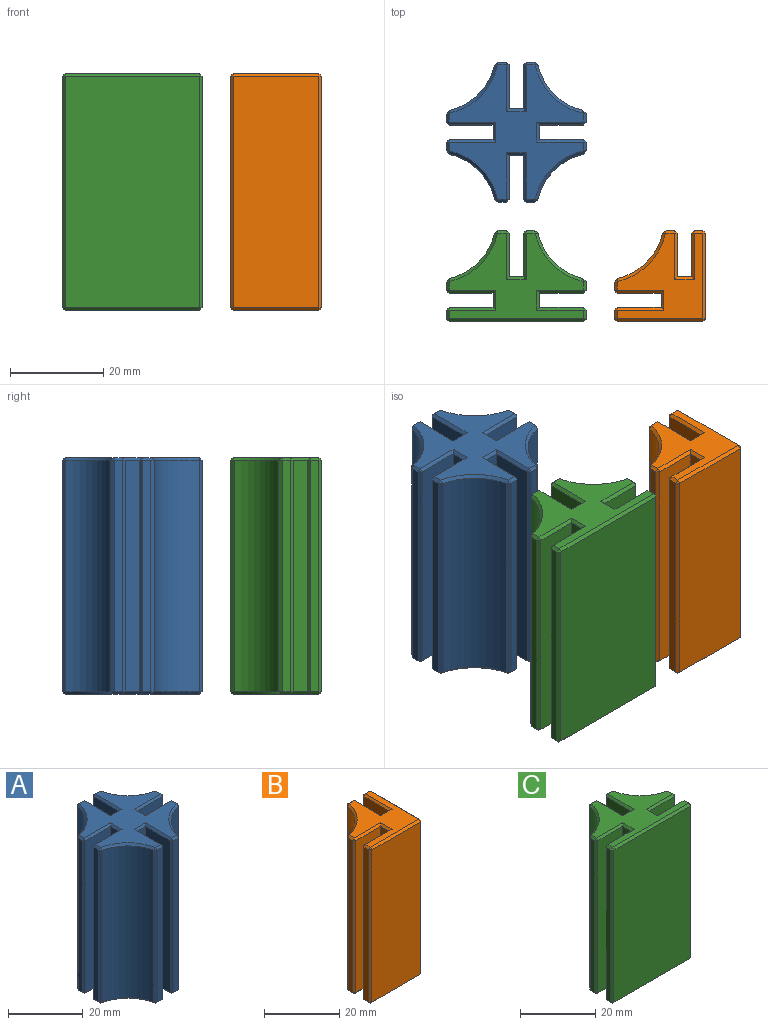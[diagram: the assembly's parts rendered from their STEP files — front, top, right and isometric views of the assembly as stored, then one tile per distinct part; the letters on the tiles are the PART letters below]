
ASSEMBLY  parts=3 mates=2
PART A: 122 faces, bbox 30x30x50.8 mm
  f0: plane 49.6x1.66mm, normal (-1,0,0), area 82.3mm2, adj f98,f106,f107,f108
  f1: plane 49.6x9.4mm, normal (0,-1,0), area 466.2mm2, adj f2,f97,f98,f99
  f2: plane 49.6x3.08mm, normal (-1,0,0), area 152.5mm2, adj f1,f3,f93,f94
  f3: plane 49.6x9.4mm, normal (0,1,0), area 466.2mm2, adj f2,f79,f88,f89
  f4: plane 49.6x1.8mm, normal (-1,0,0), area 89.3mm2, adj f69,f78,f79,f80
  f5: cylinder r=12.91mm len=49.6mm, axis (0,0,-1), area 712.6mm2, adj f59,f68,f69,f70
  f6: plane 49.6x1.66mm, normal (0,-1,0), area 82.3mm2, adj f50,f58,f59,f60
  f7: plane 49.6x9.4mm, normal (1,0,0), area 466.2mm2, adj f8,f49,f50,f51
  f8: plane 49.6x3.08mm, normal (0,-1,0), area 152.5mm2, adj f7,f9,f45,f46
  f9: plane 49.6x9.4mm, normal (-1,0,0), area 466.2mm2, adj f8,f31,f40,f41
  f10: plane 49.6x1.8mm, normal (0,-1,0), area 89.3mm2, adj f26,f30,f31,f32
  f11: cylinder r=12.91mm len=49.6mm, axis (0,0,-1), area 712.6mm2, adj f26,f29,f33,f34
  f12: plane 49.6x1.66mm, normal (1,0,0), area 82.3mm2, adj f34,f39,f42,f43
  f13: plane 49.6x9.4mm, normal (0,1,0), area 466.2mm2, adj f14,f43,f48,f52
  f14: plane 49.6x3.08mm, normal (1,0,0), area 152.5mm2, adj f13,f15,f53,f56
  f15: plane 49.6x9.4mm, normal (0,-1,0), area 466.2mm2, adj f14,f57,f61,f62
  f16: plane 49.6x1.8mm, normal (1,0,0), area 89.3mm2, adj f62,f67,f71,f72
  f17: cylinder r=12.91mm len=49.6mm, axis (0,0,-1), area 712.6mm2, adj f72,f77,f81,f82
  f18: plane 49.6x1.66mm, normal (0,1,0), area 82.3mm2, adj f82,f87,f90,f91
  f19: plane 49.6x9.4mm, normal (-1,0,0), area 466.2mm2, adj f20,f91,f96,f100
  f20: plane 49.6x3.08mm, normal (0,1,0), area 152.5mm2, adj f19,f21,f101,f104
  f21: plane 49.6x9.4mm, normal (1,0,0), area 466.2mm2, adj f20,f105,f109,f110
  f22: plane 49.6x1.8mm, normal (0,1,0), area 89.3mm2, adj f110,f115,f118,f121
  f23: cylinder r=12.91mm len=49.6mm, axis (0,0,-1), area 712.6mm2, adj f107,f116,f117,f121
  f24: plane 28.8x28.8mm, normal (0,0,1), area 358.3mm2, adj f29,f30,f39,f40,f45,f48,f49,f53
  f25: plane 28.8x28.8mm, normal (0,0,-1), area 358.3mm2, adj f32,f33,f41,f42,f46,f51,f52,f56
  f26: plane 49.6x0.76mm, normal (0.71,-0.71,0), area 53.2mm2, adj f10,f11,f27,f28
  f27: plane 0.77x0.77mm, normal (0.61,-0.61,0.5), area 0.4mm2, adj f26,f29,f30
  f28: plane 0.77x0.77mm, normal (0.61,-0.61,-0.5), area 0.4mm2, adj f26,f32,f33
  f29: cone r=13.51mm half-angle=45deg, axis (0,0,1), area 12.7mm2, adj f11,f24,f27,f35
  f30: plane 1.91x0.6mm, normal (0,-0.71,0.71), area 1.6mm2, adj f10,f24,f27,f36
  f31: plane 49.6x0.6mm, normal (-0.71,-0.71,0), area 42.1mm2, adj f9,f10,f36,f37
  f32: plane 1.91x0.6mm, normal (0,-0.71,-0.71), area 1.6mm2, adj f10,f25,f28,f37
  f33: cone r=12.91mm half-angle=45deg, axis (0,0,-1), area 12.7mm2, adj f11,f25,f28,f38
  f34: plane 49.6x0.86mm, normal (0.82,-0.57,0), area 52.2mm2, adj f11,f12,f35,f38
  f35: plane 0.87x0.61mm, normal (0.71,-0.49,0.5), area 0.4mm2, adj f29,f34,f39
  f36: plane 0.6x0.6mm, normal (-0.58,-0.58,0.58), area 0.3mm2, adj f30,f31,f40
  f37: plane 0.6x0.6mm, normal (-0.58,-0.58,-0.58), area 0.3mm2, adj f31,f32,f41
  f38: plane 0.87x0.61mm, normal (0.71,-0.49,-0.5), area 0.4mm2, adj f33,f34,f42
  f39: plane 1.91x0.6mm, normal (0.71,0,0.71), area 1.5mm2, adj f12,f24,f35,f44
  f40: plane 10x0.6mm, normal (-0.71,0,0.71), area 8.2mm2, adj f9,f24,f36,f45
  f41: plane 10x0.6mm, normal (-0.71,0,-0.71), area 8.2mm2, adj f9,f25,f37,f46
  f42: plane 1.91x0.6mm, normal (0.71,0,-0.71), area 1.5mm2, adj f12,f25,f38,f47
  f43: plane 49.6x0.6mm, normal (0.71,0.71,0), area 42.1mm2, adj f12,f13,f44,f47
  f44: plane 0.6x0.6mm, normal (0.58,0.58,0.58), area 0.3mm2, adj f39,f43,f48
  f45: plane 4.28x0.6mm, normal (0,-0.71,0.71), area 3.1mm2, adj f8,f24,f40,f49
  f46: plane 4.28x0.6mm, normal (0,-0.71,-0.71), area 3.1mm2, adj f8,f25,f41,f51
  f47: plane 0.6x0.6mm, normal (0.58,0.58,-0.58), area 0.3mm2, adj f42,f43,f52
  f48: plane 10x0.6mm, normal (0,0.71,0.71), area 8.2mm2, adj f13,f24,f44,f53
  f49: plane 10x0.6mm, normal (0.71,0,0.71), area 8.2mm2, adj f7,f24,f45,f54
  f50: plane 49.6x0.6mm, normal (0.71,-0.71,0), area 42.1mm2, adj f6,f7,f54,f55
  f51: plane 10x0.6mm, normal (0.71,0,-0.71), area 8.2mm2, adj f7,f25,f46,f55
  f52: plane 10x0.6mm, normal (0,0.71,-0.71), area 8.2mm2, adj f13,f25,f47,f56
  f53: plane 4.28x0.6mm, normal (0.71,0,0.71), area 3.1mm2, adj f14,f24,f48,f57
  f54: plane 0.6x0.6mm, normal (0.58,-0.58,0.58), area 0.3mm2, adj f49,f50,f58
  f55: plane 0.6x0.6mm, normal (0.58,-0.58,-0.58), area 0.3mm2, adj f50,f51,f60
  f56: plane 4.28x0.6mm, normal (0.71,0,-0.71), area 3.1mm2, adj f14,f25,f52,f61
  f57: plane 10x0.6mm, normal (0,-0.71,0.71), area 8.2mm2, adj f15,f24,f53,f63
  f58: plane 1.91x0.6mm, normal (0,-0.71,0.71), area 1.5mm2, adj f6,f24,f54,f64
  f59: plane 49.6x0.86mm, normal (-0.57,-0.82,0), area 52.2mm2, adj f5,f6,f64,f65
  f60: plane 1.91x0.6mm, normal (0,-0.71,-0.71), area 1.5mm2, adj f6,f25,f55,f65
  f61: plane 10x0.6mm, normal (0,-0.71,-0.71), area 8.2mm2, adj f15,f25,f56,f66
  f62: plane 49.6x0.6mm, normal (0.71,-0.71,0), area 42.1mm2, adj f15,f16,f63,f66
  f63: plane 0.6x0.6mm, normal (0.58,-0.58,0.58), area 0.3mm2, adj f57,f62,f67
  f64: plane 0.87x0.61mm, normal (-0.49,-0.71,0.5), area 0.4mm2, adj f58,f59,f68
  f65: plane 0.87x0.61mm, normal (-0.49,-0.71,-0.5), area 0.4mm2, adj f59,f60,f70
  f66: plane 0.6x0.6mm, normal (0.58,-0.58,-0.58), area 0.3mm2, adj f61,f62,f71
  f67: plane 1.91x0.6mm, normal (0.71,0,0.71), area 1.6mm2, adj f16,f24,f63,f73
  f68: cone r=13.51mm half-angle=45deg, axis (0,0,1), area 12.7mm2, adj f5,f24,f64,f74
  f69: plane 49.6x0.76mm, normal (-0.71,-0.71,0), area 53.2mm2, adj f4,f5,f74,f75
  f70: cone r=12.91mm half-angle=45deg, axis (0,0,-1), area 12.7mm2, adj f5,f25,f65,f75
  f71: plane 1.91x0.6mm, normal (0.71,0,-0.71), area 1.6mm2, adj f16,f25,f66,f76
  f72: plane 49.6x0.76mm, normal (0.71,0.71,0), area 53.2mm2, adj f16,f17,f73,f76
  f73: plane 0.77x0.77mm, normal (0.61,0.61,0.5), area 0.4mm2, adj f67,f72,f77
  f74: plane 0.77x0.77mm, normal (-0.61,-0.61,0.5), area 0.4mm2, adj f68,f69,f78
  f75: plane 0.77x0.77mm, normal (-0.61,-0.61,-0.5), area 0.4mm2, adj f69,f70,f80
  f76: plane 0.77x0.77mm, normal (0.61,0.61,-0.5), area 0.4mm2, adj f71,f72,f81
  f77: cone r=13.51mm half-angle=45deg, axis (0,0,1), area 12.7mm2, adj f17,f24,f73,f83
  f78: plane 1.91x0.6mm, normal (-0.71,0,0.71), area 1.6mm2, adj f4,f24,f74,f84
  f79: plane 49.6x0.6mm, normal (-0.71,0.71,0), area 42.1mm2, adj f3,f4,f84,f85
  f80: plane 1.91x0.6mm, normal (-0.71,0,-0.71), area 1.6mm2, adj f4,f25,f75,f85
  f81: cone r=12.91mm half-angle=45deg, axis (0,0,-1), area 12.7mm2, adj f17,f25,f76,f86
  f82: plane 49.6x0.86mm, normal (0.57,0.82,0), area 52.2mm2, adj f17,f18,f83,f86
  f83: plane 0.87x0.61mm, normal (0.49,0.71,0.5), area 0.4mm2, adj f77,f82,f87
  f84: plane 0.6x0.6mm, normal (-0.58,0.58,0.58), area 0.3mm2, adj f78,f79,f88
  f85: plane 0.6x0.6mm, normal (-0.58,0.58,-0.58), area 0.3mm2, adj f79,f80,f89
  f86: plane 0.87x0.61mm, normal (0.49,0.71,-0.5), area 0.4mm2, adj f81,f82,f90
  f87: plane 1.91x0.6mm, normal (0,0.71,0.71), area 1.5mm2, adj f18,f24,f83,f92
  f88: plane 10x0.6mm, normal (0,0.71,0.71), area 8.2mm2, adj f3,f24,f84,f93
  f89: plane 10x0.6mm, normal (0,0.71,-0.71), area 8.2mm2, adj f3,f25,f85,f94
  f90: plane 1.91x0.6mm, normal (0,0.71,-0.71), area 1.5mm2, adj f18,f25,f86,f95
  f91: plane 49.6x0.6mm, normal (-0.71,0.71,0), area 42.1mm2, adj f18,f19,f92,f95
  f92: plane 0.6x0.6mm, normal (-0.58,0.58,0.58), area 0.3mm2, adj f87,f91,f96
  f93: plane 4.28x0.6mm, normal (-0.71,0,0.71), area 3.1mm2, adj f2,f24,f88,f97
  f94: plane 4.28x0.6mm, normal (-0.71,0,-0.71), area 3.1mm2, adj f2,f25,f89,f99
  f95: plane 0.6x0.6mm, normal (-0.58,0.58,-0.58), area 0.3mm2, adj f90,f91,f100
  f96: plane 10x0.6mm, normal (-0.71,0,0.71), area 8.2mm2, adj f19,f24,f92,f101
  f97: plane 10x0.6mm, normal (0,-0.71,0.71), area 8.2mm2, adj f1,f24,f93,f102
  f98: plane 49.6x0.6mm, normal (-0.71,-0.71,0), area 42.1mm2, adj f0,f1,f102,f103
  f99: plane 10x0.6mm, normal (0,-0.71,-0.71), area 8.2mm2, adj f1,f25,f94,f103
  f100: plane 10x0.6mm, normal (-0.71,0,-0.71), area 8.2mm2, adj f19,f25,f95,f104
  f101: plane 4.28x0.6mm, normal (0,0.71,0.71), area 3.1mm2, adj f20,f24,f96,f105
  f102: plane 0.6x0.6mm, normal (-0.58,-0.58,0.58), area 0.3mm2, adj f97,f98,f106
  f103: plane 0.6x0.6mm, normal (-0.58,-0.58,-0.58), area 0.3mm2, adj f98,f99,f108
  f104: plane 4.28x0.6mm, normal (0,0.71,-0.71), area 3.1mm2, adj f20,f25,f100,f109
  f105: plane 10x0.6mm, normal (0.71,0,0.71), area 8.2mm2, adj f21,f24,f101,f111
  f106: plane 1.91x0.6mm, normal (-0.71,0,0.71), area 1.5mm2, adj f0,f24,f102,f112
  f107: plane 49.6x0.86mm, normal (-0.82,0.57,0), area 52.2mm2, adj f0,f23,f112,f113
  f108: plane 1.91x0.6mm, normal (-0.71,0,-0.71), area 1.5mm2, adj f0,f25,f103,f113
  f109: plane 10x0.6mm, normal (0.71,0,-0.71), area 8.2mm2, adj f21,f25,f104,f114
  f110: plane 49.6x0.6mm, normal (0.71,0.71,0), area 42.1mm2, adj f21,f22,f111,f114
  f111: plane 0.6x0.6mm, normal (0.58,0.58,0.58), area 0.3mm2, adj f105,f110,f115
  f112: plane 0.87x0.61mm, normal (-0.71,0.49,0.5), area 0.4mm2, adj f106,f107,f116
  f113: plane 0.87x0.61mm, normal (-0.71,0.49,-0.5), area 0.4mm2, adj f107,f108,f117
  f114: plane 0.6x0.6mm, normal (0.58,0.58,-0.58), area 0.3mm2, adj f109,f110,f118
  f115: plane 1.91x0.6mm, normal (0,0.71,0.71), area 1.6mm2, adj f22,f24,f111,f119
  f116: cone r=13.51mm half-angle=45deg, axis (0,0,1), area 12.7mm2, adj f23,f24,f112,f119
  f117: cone r=12.91mm half-angle=45deg, axis (0,0,-1), area 12.7mm2, adj f23,f25,f113,f120
  f118: plane 1.91x0.6mm, normal (0,0.71,-0.71), area 1.6mm2, adj f22,f25,f114,f120
  f119: plane 0.77x0.77mm, normal (-0.61,0.61,0.5), area 0.4mm2, adj f115,f116,f121
  f120: plane 0.77x0.77mm, normal (-0.61,0.61,-0.5), area 0.4mm2, adj f117,f118,f121
  f121: plane 49.6x0.76mm, normal (-0.71,0.71,0), area 53.2mm2, adj f22,f23,f119,f120
PART B: 68 faces, bbox 19.5x19.5x50.8 mm
  f0: plane 49.6x1.66mm, normal (-1,0,0), area 82.3mm2, adj f44,f52,f53,f54
  f1: plane 49.6x9.4mm, normal (0,-1,0), area 466.2mm2, adj f2,f43,f44,f45
  f2: plane 49.6x3.08mm, normal (-1,0,0), area 152.5mm2, adj f1,f3,f39,f40
  f3: plane 49.6x9.4mm, normal (0,1,0), area 466.2mm2, adj f2,f25,f34,f35
  f4: plane 49.6x1.8mm, normal (-1,0,0), area 89.3mm2, adj f16,f24,f25,f26
  f5: plane 49.6x18.34mm, normal (0,-1,0), area 909.5mm2, adj f15,f16,f17,f18
  f6: plane 49.6x18.34mm, normal (1,0,0), area 909.5mm2, adj f18,f23,f27,f28
  f7: plane 49.6x1.8mm, normal (0,1,0), area 89.3mm2, adj f28,f33,f36,f37
  f8: plane 49.6x9.4mm, normal (-1,0,0), area 466.2mm2, adj f9,f37,f42,f46
  f9: plane 49.6x3.08mm, normal (0,1,0), area 152.5mm2, adj f8,f10,f47,f50
  f10: plane 49.6x9.4mm, normal (1,0,0), area 466.2mm2, adj f9,f51,f55,f56
  f11: plane 49.6x1.8mm, normal (0,1,0), area 89.3mm2, adj f56,f61,f64,f67
  f12: cylinder r=12.91mm len=49.6mm, axis (0,0,-1), area 712.6mm2, adj f53,f62,f63,f67
  f13: plane 18.34x18.34mm, normal (0,0,1), area 175.7mm2, adj f15,f23,f24,f33,f34,f39,f42,f43
  f14: plane 18.34x18.34mm, normal (0,0,-1), area 175.7mm2, adj f17,f26,f27,f35,f36,f40,f45,f46
  f15: plane 18.34x0.6mm, normal (0,-0.71,0.71), area 15.6mm2, adj f5,f13,f19,f20
  f16: plane 49.6x0.6mm, normal (-0.71,-0.71,0), area 42.1mm2, adj f4,f5,f20,f21
  f17: plane 18.34x0.6mm, normal (0,-0.71,-0.71), area 15.6mm2, adj f5,f14,f21,f22
  f18: plane 49.6x0.6mm, normal (0.71,-0.71,0), area 42.1mm2, adj f5,f6,f19,f22
  f19: plane 0.6x0.6mm, normal (0.58,-0.58,0.58), area 0.3mm2, adj f15,f18,f23
  f20: plane 0.6x0.6mm, normal (-0.58,-0.58,0.58), area 0.3mm2, adj f15,f16,f24
  f21: plane 0.6x0.6mm, normal (-0.58,-0.58,-0.58), area 0.3mm2, adj f16,f17,f26
  f22: plane 0.6x0.6mm, normal (0.58,-0.58,-0.58), area 0.3mm2, adj f17,f18,f27
  f23: plane 18.34x0.6mm, normal (0.71,0,0.71), area 15.6mm2, adj f6,f13,f19,f29
  f24: plane 1.8x0.6mm, normal (-0.71,0,0.71), area 1.5mm2, adj f4,f13,f20,f30
  f25: plane 49.6x0.6mm, normal (-0.71,0.71,0), area 42.1mm2, adj f3,f4,f30,f31
  f26: plane 1.8x0.6mm, normal (-0.71,0,-0.71), area 1.5mm2, adj f4,f14,f21,f31
  f27: plane 18.34x0.6mm, normal (0.71,0,-0.71), area 15.6mm2, adj f6,f14,f22,f32
  f28: plane 49.6x0.6mm, normal (0.71,0.71,0), area 42.1mm2, adj f6,f7,f29,f32
  f29: plane 0.6x0.6mm, normal (0.58,0.58,0.58), area 0.3mm2, adj f23,f28,f33
  f30: plane 0.6x0.6mm, normal (-0.58,0.58,0.58), area 0.3mm2, adj f24,f25,f34
  f31: plane 0.6x0.6mm, normal (-0.58,0.58,-0.58), area 0.3mm2, adj f25,f26,f35
  f32: plane 0.6x0.6mm, normal (0.58,0.58,-0.58), area 0.3mm2, adj f27,f28,f36
  f33: plane 1.8x0.6mm, normal (0,0.71,0.71), area 1.5mm2, adj f7,f13,f29,f38
  f34: plane 10x0.6mm, normal (0,0.71,0.71), area 8.2mm2, adj f3,f13,f30,f39
  f35: plane 10x0.6mm, normal (0,0.71,-0.71), area 8.2mm2, adj f3,f14,f31,f40
  f36: plane 1.8x0.6mm, normal (0,0.71,-0.71), area 1.5mm2, adj f7,f14,f32,f41
  f37: plane 49.6x0.6mm, normal (-0.71,0.71,0), area 42.1mm2, adj f7,f8,f38,f41
  f38: plane 0.6x0.6mm, normal (-0.58,0.58,0.58), area 0.3mm2, adj f33,f37,f42
  f39: plane 4.28x0.6mm, normal (-0.71,0,0.71), area 3.1mm2, adj f2,f13,f34,f43
  f40: plane 4.28x0.6mm, normal (-0.71,0,-0.71), area 3.1mm2, adj f2,f14,f35,f45
  f41: plane 0.6x0.6mm, normal (-0.58,0.58,-0.58), area 0.3mm2, adj f36,f37,f46
  f42: plane 10x0.6mm, normal (-0.71,0,0.71), area 8.2mm2, adj f8,f13,f38,f47
  f43: plane 10x0.6mm, normal (0,-0.71,0.71), area 8.2mm2, adj f1,f13,f39,f48
  f44: plane 49.6x0.6mm, normal (-0.71,-0.71,0), area 42.1mm2, adj f0,f1,f48,f49
  f45: plane 10x0.6mm, normal (0,-0.71,-0.71), area 8.2mm2, adj f1,f14,f40,f49
  f46: plane 10x0.6mm, normal (-0.71,0,-0.71), area 8.2mm2, adj f8,f14,f41,f50
  f47: plane 4.28x0.6mm, normal (0,0.71,0.71), area 3.1mm2, adj f9,f13,f42,f51
  f48: plane 0.6x0.6mm, normal (-0.58,-0.58,0.58), area 0.3mm2, adj f43,f44,f52
  f49: plane 0.6x0.6mm, normal (-0.58,-0.58,-0.58), area 0.3mm2, adj f44,f45,f54
  f50: plane 4.28x0.6mm, normal (0,0.71,-0.71), area 3.1mm2, adj f9,f14,f46,f55
  f51: plane 10x0.6mm, normal (0.71,0,0.71), area 8.2mm2, adj f10,f13,f47,f57
  f52: plane 1.91x0.6mm, normal (-0.71,0,0.71), area 1.5mm2, adj f0,f13,f48,f58
  f53: plane 49.6x0.86mm, normal (-0.82,0.57,0), area 52.2mm2, adj f0,f12,f58,f59
  f54: plane 1.91x0.6mm, normal (-0.71,0,-0.71), area 1.5mm2, adj f0,f14,f49,f59
  f55: plane 10x0.6mm, normal (0.71,0,-0.71), area 8.2mm2, adj f10,f14,f50,f60
  f56: plane 49.6x0.6mm, normal (0.71,0.71,0), area 42.1mm2, adj f10,f11,f57,f60
  f57: plane 0.6x0.6mm, normal (0.58,0.58,0.58), area 0.3mm2, adj f51,f56,f61
  f58: plane 0.87x0.61mm, normal (-0.71,0.49,0.5), area 0.4mm2, adj f52,f53,f62
  f59: plane 0.87x0.61mm, normal (-0.71,0.49,-0.5), area 0.4mm2, adj f53,f54,f63
  f60: plane 0.6x0.6mm, normal (0.58,0.58,-0.58), area 0.3mm2, adj f55,f56,f64
  f61: plane 1.91x0.6mm, normal (0,0.71,0.71), area 1.6mm2, adj f11,f13,f57,f65
  f62: cone r=13.51mm half-angle=45deg, axis (0,0,1), area 12.7mm2, adj f12,f13,f58,f65
  f63: cone r=12.91mm half-angle=45deg, axis (0,0,-1), area 12.7mm2, adj f12,f14,f59,f66
  f64: plane 1.91x0.6mm, normal (0,0.71,-0.71), area 1.6mm2, adj f11,f14,f60,f66
  f65: plane 0.77x0.77mm, normal (-0.61,0.61,0.5), area 0.4mm2, adj f61,f62,f67
  f66: plane 0.77x0.77mm, normal (-0.61,0.61,-0.5), area 0.4mm2, adj f63,f64,f67
  f67: plane 49.6x0.76mm, normal (-0.71,0.71,0), area 53.2mm2, adj f11,f12,f65,f66
PART C: 92 faces, bbox 30x19.5x50.8 mm
  f0: plane 49.6x1.66mm, normal (-1,0,0), area 82.3mm2, adj f68,f76,f77,f78
  f1: plane 49.6x9.4mm, normal (0,-1,0), area 466.2mm2, adj f2,f67,f68,f69
  f2: plane 49.6x3.08mm, normal (-1,0,0), area 152.5mm2, adj f1,f3,f63,f64
  f3: plane 49.6x9.4mm, normal (0,1,0), area 466.2mm2, adj f2,f49,f58,f59
  f4: plane 49.6x1.8mm, normal (-1,0,0), area 89.3mm2, adj f39,f48,f49,f50
  f5: plane 49.6x28.8mm, normal (0,-1,0), area 1428.5mm2, adj f29,f38,f39,f40
  f6: plane 49.6x1.8mm, normal (1,0,0), area 89.3mm2, adj f21,f28,f29,f30
  f7: plane 49.6x9.4mm, normal (0,1,0), area 466.2mm2, adj f8,f20,f21,f22
  f8: plane 49.6x3.08mm, normal (1,0,0), area 152.5mm2, adj f7,f9,f23,f26
  f9: plane 49.6x9.4mm, normal (0,-1,0), area 466.2mm2, adj f8,f27,f31,f32
  f10: plane 49.6x1.8mm, normal (1,0,0), area 89.3mm2, adj f32,f37,f41,f42
  f11: cylinder r=12.91mm len=49.6mm, axis (0,0,-1), area 712.6mm2, adj f42,f47,f51,f52
  f12: plane 49.6x1.66mm, normal (0,1,0), area 82.3mm2, adj f52,f57,f60,f61
  f13: plane 49.6x9.4mm, normal (-1,0,0), area 466.2mm2, adj f14,f61,f66,f70
  f14: plane 49.6x3.08mm, normal (0,1,0), area 152.5mm2, adj f13,f15,f71,f74
  f15: plane 49.6x9.4mm, normal (1,0,0), area 466.2mm2, adj f14,f75,f79,f80
  f16: plane 49.6x1.8mm, normal (0,1,0), area 89.3mm2, adj f80,f85,f88,f91
  f17: cylinder r=12.91mm len=49.6mm, axis (0,0,-1), area 712.6mm2, adj f77,f86,f87,f91
  f18: plane 28.8x18.34mm, normal (0,0,1), area 249.8mm2, adj f20,f23,f27,f28,f37,f38,f47,f48
  f19: plane 28.8x18.34mm, normal (0,0,-1), area 249.8mm2, adj f22,f26,f30,f31,f40,f41,f50,f51
  f20: plane 10x0.6mm, normal (0,0.71,0.71), area 8.2mm2, adj f7,f18,f23,f24
  f21: plane 49.6x0.6mm, normal (0.71,0.71,0), area 42.1mm2, adj f6,f7,f24,f25
  f22: plane 10x0.6mm, normal (0,0.71,-0.71), area 8.2mm2, adj f7,f19,f25,f26
  f23: plane 4.28x0.6mm, normal (0.71,0,0.71), area 3.1mm2, adj f8,f18,f20,f27
  f24: plane 0.6x0.6mm, normal (0.58,0.58,0.58), area 0.3mm2, adj f20,f21,f28
  f25: plane 0.6x0.6mm, normal (0.58,0.58,-0.58), area 0.3mm2, adj f21,f22,f30
  f26: plane 4.28x0.6mm, normal (0.71,0,-0.71), area 3.1mm2, adj f8,f19,f22,f31
  f27: plane 10x0.6mm, normal (0,-0.71,0.71), area 8.2mm2, adj f9,f18,f23,f33
  f28: plane 1.8x0.6mm, normal (0.71,0,0.71), area 1.5mm2, adj f6,f18,f24,f34
  f29: plane 49.6x0.6mm, normal (0.71,-0.71,0), area 42.1mm2, adj f5,f6,f34,f35
  f30: plane 1.8x0.6mm, normal (0.71,0,-0.71), area 1.5mm2, adj f6,f19,f25,f35
  f31: plane 10x0.6mm, normal (0,-0.71,-0.71), area 8.2mm2, adj f9,f19,f26,f36
  f32: plane 49.6x0.6mm, normal (0.71,-0.71,0), area 42.1mm2, adj f9,f10,f33,f36
  f33: plane 0.6x0.6mm, normal (0.58,-0.58,0.58), area 0.3mm2, adj f27,f32,f37
  f34: plane 0.6x0.6mm, normal (0.58,-0.58,0.58), area 0.3mm2, adj f28,f29,f38
  f35: plane 0.6x0.6mm, normal (0.58,-0.58,-0.58), area 0.3mm2, adj f29,f30,f40
  f36: plane 0.6x0.6mm, normal (0.58,-0.58,-0.58), area 0.3mm2, adj f31,f32,f41
  f37: plane 1.91x0.6mm, normal (0.71,0,0.71), area 1.6mm2, adj f10,f18,f33,f43
  f38: plane 28.8x0.6mm, normal (0,-0.71,0.71), area 24.4mm2, adj f5,f18,f34,f44
  f39: plane 49.6x0.6mm, normal (-0.71,-0.71,0), area 42.1mm2, adj f4,f5,f44,f45
  f40: plane 28.8x0.6mm, normal (0,-0.71,-0.71), area 24.4mm2, adj f5,f19,f35,f45
  f41: plane 1.91x0.6mm, normal (0.71,0,-0.71), area 1.6mm2, adj f10,f19,f36,f46
  f42: plane 49.6x0.76mm, normal (0.71,0.71,0), area 53.2mm2, adj f10,f11,f43,f46
  f43: plane 0.77x0.77mm, normal (0.61,0.61,0.5), area 0.4mm2, adj f37,f42,f47
  f44: plane 0.6x0.6mm, normal (-0.58,-0.58,0.58), area 0.3mm2, adj f38,f39,f48
  f45: plane 0.6x0.6mm, normal (-0.58,-0.58,-0.58), area 0.3mm2, adj f39,f40,f50
  f46: plane 0.77x0.77mm, normal (0.61,0.61,-0.5), area 0.4mm2, adj f41,f42,f51
  f47: cone r=13.51mm half-angle=45deg, axis (0,0,1), area 12.7mm2, adj f11,f18,f43,f53
  f48: plane 1.8x0.6mm, normal (-0.71,0,0.71), area 1.5mm2, adj f4,f18,f44,f54
  f49: plane 49.6x0.6mm, normal (-0.71,0.71,0), area 42.1mm2, adj f3,f4,f54,f55
  f50: plane 1.8x0.6mm, normal (-0.71,0,-0.71), area 1.5mm2, adj f4,f19,f45,f55
  f51: cone r=12.91mm half-angle=45deg, axis (0,0,-1), area 12.7mm2, adj f11,f19,f46,f56
  f52: plane 49.6x0.86mm, normal (0.57,0.82,0), area 52.2mm2, adj f11,f12,f53,f56
  f53: plane 0.87x0.61mm, normal (0.49,0.71,0.5), area 0.4mm2, adj f47,f52,f57
  f54: plane 0.6x0.6mm, normal (-0.58,0.58,0.58), area 0.3mm2, adj f48,f49,f58
  f55: plane 0.6x0.6mm, normal (-0.58,0.58,-0.58), area 0.3mm2, adj f49,f50,f59
  f56: plane 0.87x0.61mm, normal (0.49,0.71,-0.5), area 0.4mm2, adj f51,f52,f60
  f57: plane 1.91x0.6mm, normal (0,0.71,0.71), area 1.5mm2, adj f12,f18,f53,f62
  f58: plane 10x0.6mm, normal (0,0.71,0.71), area 8.2mm2, adj f3,f18,f54,f63
  f59: plane 10x0.6mm, normal (0,0.71,-0.71), area 8.2mm2, adj f3,f19,f55,f64
  f60: plane 1.91x0.6mm, normal (0,0.71,-0.71), area 1.5mm2, adj f12,f19,f56,f65
  f61: plane 49.6x0.6mm, normal (-0.71,0.71,0), area 42.1mm2, adj f12,f13,f62,f65
  f62: plane 0.6x0.6mm, normal (-0.58,0.58,0.58), area 0.3mm2, adj f57,f61,f66
  f63: plane 4.28x0.6mm, normal (-0.71,0,0.71), area 3.1mm2, adj f2,f18,f58,f67
  f64: plane 4.28x0.6mm, normal (-0.71,0,-0.71), area 3.1mm2, adj f2,f19,f59,f69
  f65: plane 0.6x0.6mm, normal (-0.58,0.58,-0.58), area 0.3mm2, adj f60,f61,f70
  f66: plane 10x0.6mm, normal (-0.71,0,0.71), area 8.2mm2, adj f13,f18,f62,f71
  f67: plane 10x0.6mm, normal (0,-0.71,0.71), area 8.2mm2, adj f1,f18,f63,f72
  f68: plane 49.6x0.6mm, normal (-0.71,-0.71,0), area 42.1mm2, adj f0,f1,f72,f73
  f69: plane 10x0.6mm, normal (0,-0.71,-0.71), area 8.2mm2, adj f1,f19,f64,f73
  f70: plane 10x0.6mm, normal (-0.71,0,-0.71), area 8.2mm2, adj f13,f19,f65,f74
  f71: plane 4.28x0.6mm, normal (0,0.71,0.71), area 3.1mm2, adj f14,f18,f66,f75
  f72: plane 0.6x0.6mm, normal (-0.58,-0.58,0.58), area 0.3mm2, adj f67,f68,f76
  f73: plane 0.6x0.6mm, normal (-0.58,-0.58,-0.58), area 0.3mm2, adj f68,f69,f78
  f74: plane 4.28x0.6mm, normal (0,0.71,-0.71), area 3.1mm2, adj f14,f19,f70,f79
  f75: plane 10x0.6mm, normal (0.71,0,0.71), area 8.2mm2, adj f15,f18,f71,f81
  f76: plane 1.91x0.6mm, normal (-0.71,0,0.71), area 1.5mm2, adj f0,f18,f72,f82
  f77: plane 49.6x0.86mm, normal (-0.82,0.57,0), area 52.2mm2, adj f0,f17,f82,f83
  f78: plane 1.91x0.6mm, normal (-0.71,0,-0.71), area 1.5mm2, adj f0,f19,f73,f83
  f79: plane 10x0.6mm, normal (0.71,0,-0.71), area 8.2mm2, adj f15,f19,f74,f84
  f80: plane 49.6x0.6mm, normal (0.71,0.71,0), area 42.1mm2, adj f15,f16,f81,f84
  f81: plane 0.6x0.6mm, normal (0.58,0.58,0.58), area 0.3mm2, adj f75,f80,f85
  f82: plane 0.87x0.61mm, normal (-0.71,0.49,0.5), area 0.4mm2, adj f76,f77,f86
  f83: plane 0.87x0.61mm, normal (-0.71,0.49,-0.5), area 0.4mm2, adj f77,f78,f87
  f84: plane 0.6x0.6mm, normal (0.58,0.58,-0.58), area 0.3mm2, adj f79,f80,f88
  f85: plane 1.91x0.6mm, normal (0,0.71,0.71), area 1.6mm2, adj f16,f18,f81,f89
  f86: cone r=13.51mm half-angle=45deg, axis (0,0,1), area 12.7mm2, adj f17,f18,f82,f89
  f87: cone r=12.91mm half-angle=45deg, axis (0,0,-1), area 12.7mm2, adj f17,f19,f83,f90
  f88: plane 1.91x0.6mm, normal (0,0.71,-0.71), area 1.6mm2, adj f16,f19,f84,f90
  f89: plane 0.77x0.77mm, normal (-0.61,0.61,0.5), area 0.4mm2, adj f85,f86,f91
  f90: plane 0.77x0.77mm, normal (-0.61,0.61,-0.5), area 0.4mm2, adj f87,f88,f91
  f91: plane 49.6x0.76mm, normal (-0.71,0.71,0), area 53.2mm2, adj f16,f17,f89,f90
PLACE A t=(0,40,-50.8)mm
PLACE B t=(36.06,3.94,-50.8)mm
PLACE C t=(0,3.94,-50.8)mm
MATE fastened B.f13 <-> C.f18  axis (0,0,1) through (40,0,0)mm
MATE fastened A.f24 <-> C.f18  axis (0,0,1) through (0,40,0)mm
